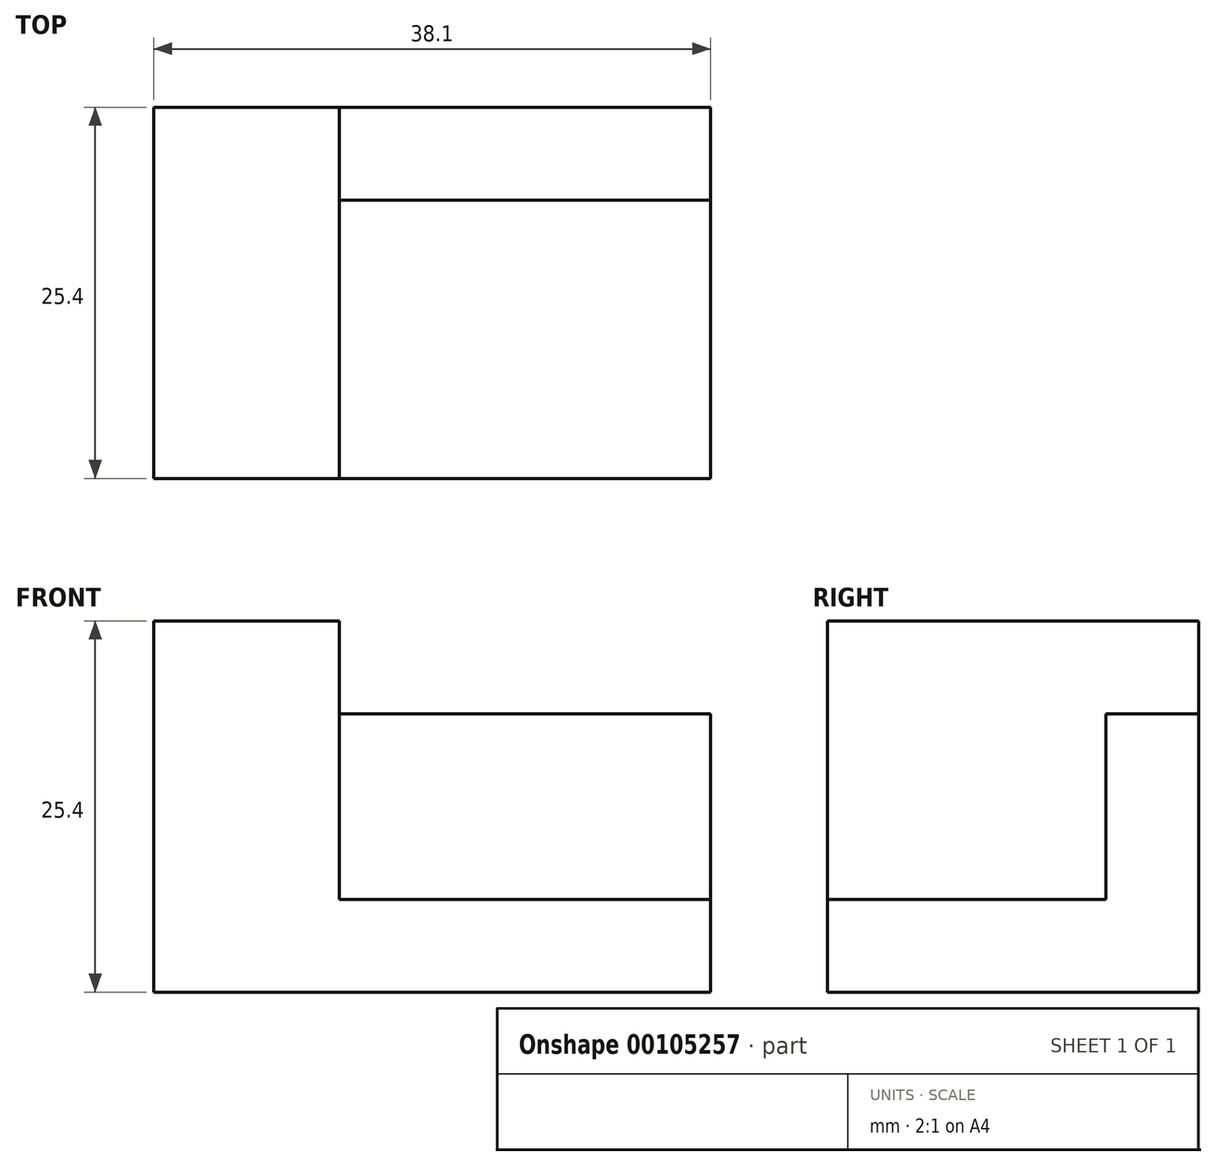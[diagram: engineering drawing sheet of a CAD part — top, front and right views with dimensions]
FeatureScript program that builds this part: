
annotation { "Feature Type Name" : "Feature", "Feature Type Description" : "" }
export const myFeature = defineFeature(function(context is Context, id is Id, definition is map)
    precondition{}
    {
        {
            var Q0;
            Q0=qCreatedBy(makeId("Front.planeOp"),FACE);
            var sketch = newSketch(context, id + "F0", { "sketchPlane" : qUnion([Q0])});
            skLineSegment(sketch, "E0", {"start": v(0, 0) * mm, "end": v(0, 25.4) * mm});
            skLineSegment(sketch, "E1", {"start": v(0, 25.4) * mm, "end": v(12.7, 25.4) * mm});
            skLineSegment(sketch, "E2", {"start": v(12.7, 25.4) * mm, "end": v(12.7, 6.35) * mm});
            skLineSegment(sketch, "E3", {"start": v(12.7, 6.35) * mm, "end": v(38.1, 6.35) * mm});
            skLineSegment(sketch, "E4", {"start": v(38.1, 6.35) * mm, "end": v(38.1, 0) * mm});
            skLineSegment(sketch, "E5", {"start": v(38.1, 0) * mm, "end": v(0, 0) * mm});
            skSolve(sketch);
        }
        {
            var Q0;
            Q0 = qSketchRegion(id + "F0", true);
            extrude(context, id + "F1", {"entities" : qUnion([Q0]), "depth" : 25.4 * mm});
        }
        {
            var Q0;
            Q0=qCreatedBy(makeId("Right.planeOp"),FACE);
            var sketch = newSketch(context, id + "F2", { "sketchPlane" : qUnion([Q0])});
            skLineSegment(sketch, "E6.bottom", {"start": v(0, 6.35) * mm, "end": v(-6.35, 6.35) * mm});
            skLineSegment(sketch, "E6.top", {"start": v(0, 19.05) * mm, "end": v(-6.35, 19.05) * mm});
            skLineSegment(sketch, "E6.left", {"start": v(0, 6.35) * mm, "end": v(0, 19.05) * mm});
            skLineSegment(sketch, "E6.right", {"start": v(-6.35, 6.35) * mm, "end": v(-6.35, 19.05) * mm});
            skSolve(sketch);
        }
        {
            var Q0;
            Q0 = qSketchRegion(id + "F2", true);
            extrude(context, id + "F3", {"entities" : qUnion([Q0]), "operationType" : NewBodyOperationType.ADD, "depth" : 38.1 * mm});
        }
    });
